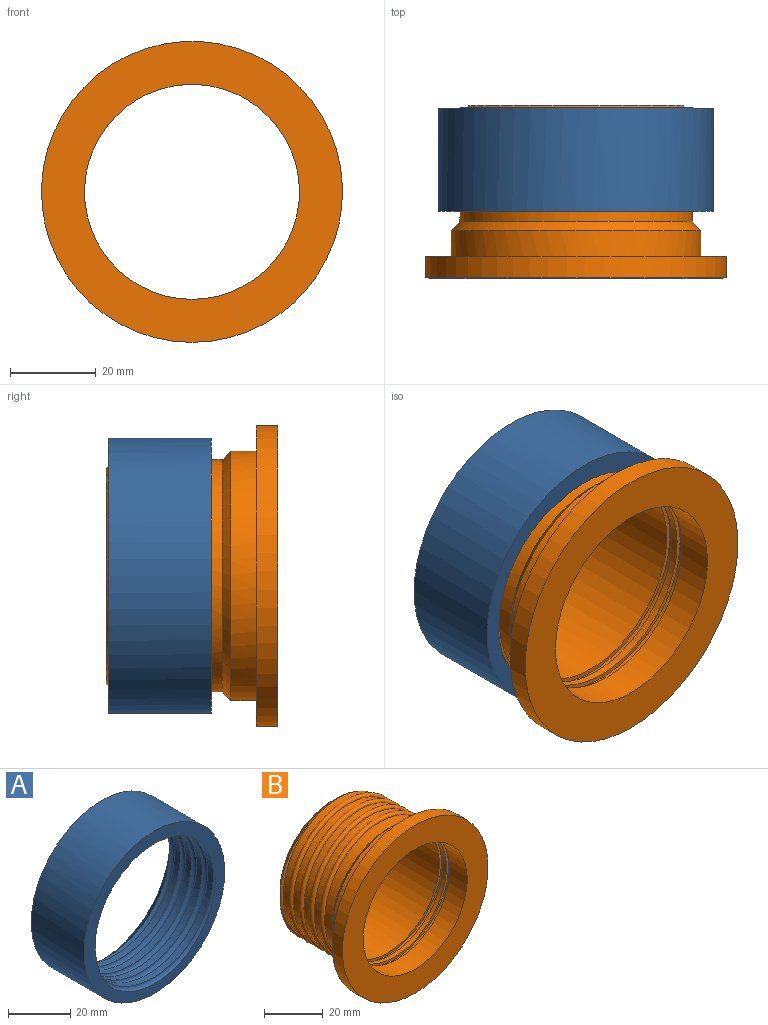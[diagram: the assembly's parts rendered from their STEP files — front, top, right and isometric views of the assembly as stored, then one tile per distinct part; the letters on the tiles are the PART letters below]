
ASSEMBLY  parts=2 mates=1
PART A: 7 faces, bbox 64x26.2x64 mm
  f0: bspline ~56.39x56.33mm, area 2729.6mm2, adj f1,f2,f3,f4
  f1: plane 0.68x0.22mm, normal (0,0,-1), area 0.1mm2, adj f0,f2,f3
  f2: cylinder r=27mm len=54mm, axis (0,-1,0), area 1774mm2, adj f0,f1,f3,f4
  f3: plane 64x64mm, normal (0,-1,0), area 851.7mm2, adj f0,f1,f2,f6
  f4: cone r=33mm half-angle=45deg, axis (0,1,0), area 940mm2, adj f0,f2,f5
  f5: plane 64x64mm, normal (0,1,0), area 197.9mm2, adj f4,f6
  f6: cylinder r=32mm len=64mm, axis (0,-1,0), area 4825.5mm2, adj f3,f5
PART B: 23 faces, bbox 70.6x40.6x70.6 mm
  f0: cylinder r=29mm len=58mm, axis (0,-1,0), area 1093.3mm2, adj f10,f22
  f1: cylinder r=25mm len=50mm, axis (0,-1,0), area 1319.5mm2, adj f2,f12
  f2: plane 52x52mm, normal (0,1,0), area 160.2mm2, adj f1,f3
  f3: cylinder r=26mm len=52mm, axis (0,-1,0), area 261.4mm2, adj f2,f4
  f4: plane 52x52mm, normal (0,-1,0), area 160.2mm2, adj f3,f5
  f5: cylinder r=25mm len=50mm, axis (0,-1,0), area 282.7mm2, adj f4,f6
  f6: plane 52x52mm, normal (0,1,0), area 160.2mm2, adj f5,f7
  f7: cylinder r=26mm len=52mm, axis (0,-1,0), area 261.4mm2, adj f6,f8
  f8: plane 52x52mm, normal (0,-1,0), area 160.2mm2, adj f7,f9
  f9: cylinder r=25mm len=50mm, axis (0,-1,0), area 4178.3mm2, adj f8,f14
  f10: plane 70x70mm, normal (0,1,0), area 1206.4mm2, adj f0,f11
  f11: cylinder r=35mm len=70mm, axis (0,-1,0), area 1099.6mm2, adj f10,f12
  f12: plane 70x70mm, normal (0,-1,0), area 1885mm2, adj f1,f11
  f13: plane 49.8x28.58mm, normal (0,-1,0), area 54.2mm2, adj f15,f20
  f14: cone r=23mm half-angle=45deg, axis (0,-1,0), area 517.2mm2, adj f9,f15,f16,f21
  f15: bspline ~55.99x55.95mm, area 2331.5mm2, adj f13,f14,f16,f17,f18,f19,f20,f21
  f16: cylinder r=27mm len=54mm, axis (0,-1,0), area 423.4mm2, adj f14,f15,f17,f21
  f17: cylinder r=27mm len=54mm, axis (0,-1,0), area 508.9mm2, adj f15,f16,f18
  f18: cylinder r=27mm len=54mm, axis (0,-1,0), area 508.9mm2, adj f15,f17,f19
  f19: cylinder r=27mm len=54mm, axis (0,-1,0), area 508.9mm2, adj f15,f18,f20
  f20: cylinder r=27mm len=54mm, axis (0,-1,0), area 788.6mm2, adj f13,f15,f19,f22
  f21: cylinder r=27mm len=21.92mm, axis (0,-1,0), area 9.6mm2, adj f14,f15,f16
  f22: cone r=29mm half-angle=45deg, axis (0,-1,0), area 497.6mm2, adj f0,f20
PLACE A rot(axis=(0,1,0),90deg) t=(0.7,-10.53,13.9)mm
PLACE B t=(0.7,-10.03,13.9)mm
MATE fastened A.f2 <-> B.f0  axis (0,-1,0) through (0.7,-24.53,13.9)mm
